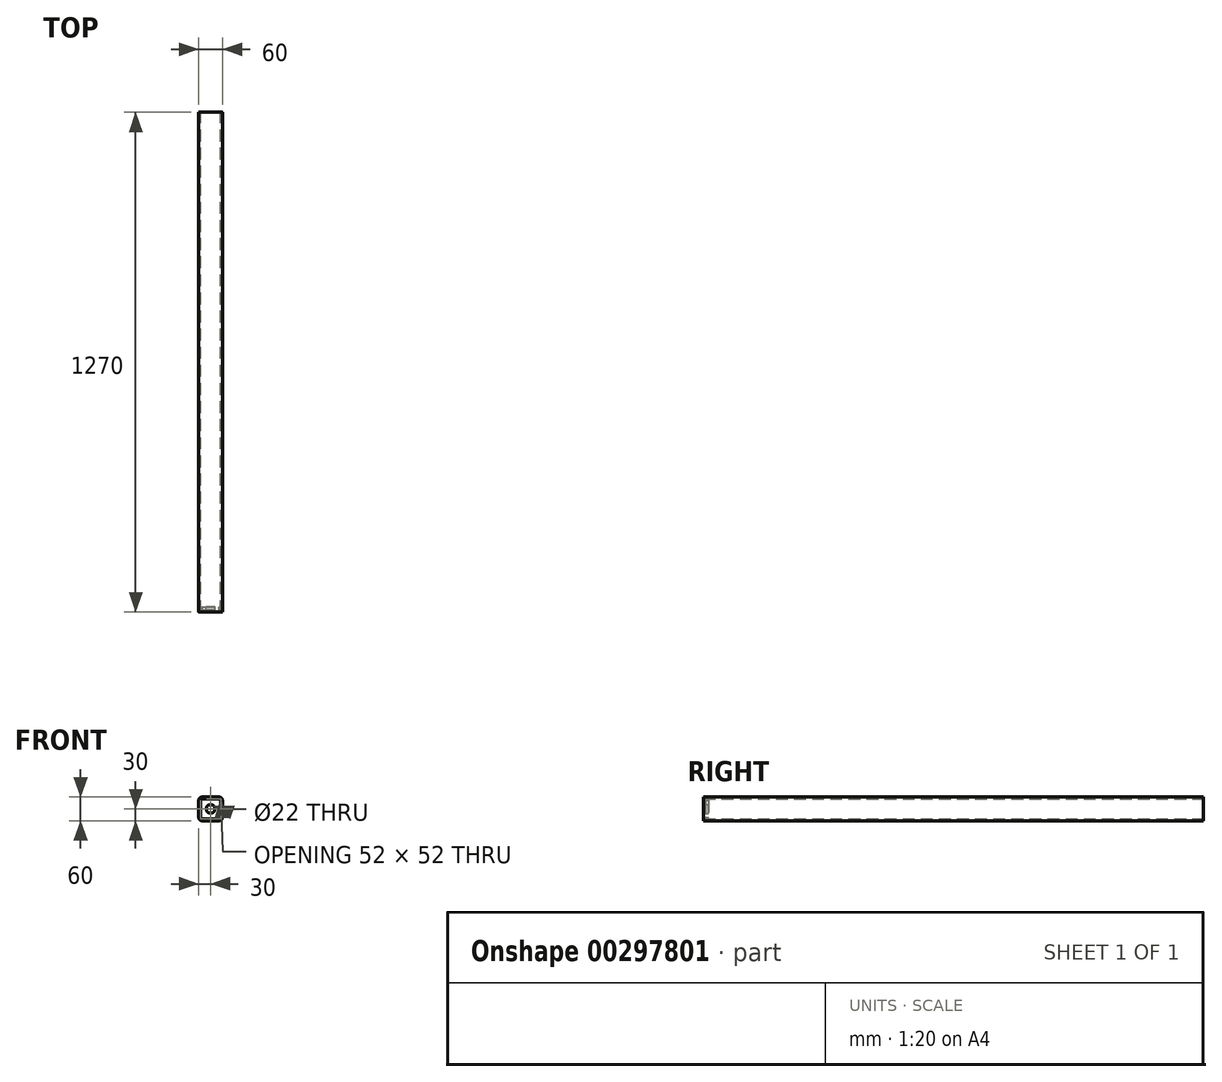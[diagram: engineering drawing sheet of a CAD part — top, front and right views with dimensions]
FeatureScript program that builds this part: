
annotation { "Feature Type Name" : "Feature", "Feature Type Description" : "" }
export const myFeature = defineFeature(function(context is Context, id is Id, definition is map)
    precondition{}
    {
        {
            var Q0;
            Q0=qCreatedBy(makeId("Front.planeOp"),FACE);
            var sketch = newSketch(context, id + "F0", { "sketchPlane" : qUnion([Q0])});
            skLineSegment(sketch, "E0.bottom", {"start": v(-22.05, 30) * mm, "end": v(22.05, 30) * mm});
            skLineSegment(sketch, "E0.top", {"start": v(-22.05, -30) * mm, "end": v(22.05, -30) * mm});
            skLineSegment(sketch, "E0.left", {"start": v(-30, 22.05) * mm, "end": v(-30, -22.05) * mm});
            skLineSegment(sketch, "E0.right", {"start": v(30, 22.05) * mm, "end": v(30, -22.05) * mm});
            skPoint(sketch, "E1.visualSharp", {"position": v(0, 0) * mm});
            skArc(sketch, "E1.filletArc", {"start": v(-22.05, 30) * mm, "mid": v(-27.67, 27.67) * mm, "end": v(-30, 22.05) * mm});
            skPoint(sketch, "E2.visualSharp", {"position": v(30, 30) * mm});
            skArc(sketch, "E2.filletArc", {"start": v(30, 22.05) * mm, "mid": v(27.67, 27.67) * mm, "end": v(22.05, 30) * mm});
            skPoint(sketch, "E3.visualSharp", {"position": v(30, -30) * mm});
            skArc(sketch, "E3.filletArc", {"start": v(22.05, -30) * mm, "mid": v(27.67, -27.67) * mm, "end": v(30, -22.05) * mm});
            skPoint(sketch, "E4.visualSharp", {"position": v(-30, -30) * mm});
            skArc(sketch, "E4.filletArc", {"start": v(-30, -22.05) * mm, "mid": v(-27.67, -27.67) * mm, "end": v(-22.05, -30) * mm});
            skArc(sketch, "E5.0", {"start": v(26, 22.05) * mm, "mid": v(24.84, 24.84) * mm, "end": v(22.05, 26) * mm});
            skLineSegment(sketch, "E5.1", {"start": v(-22.05, 26) * mm, "end": v(22.05, 26) * mm});
            skLineSegment(sketch, "E5.2", {"start": v(26, 22.05) * mm, "end": v(26, -22.05) * mm});
            skArc(sketch, "E5.3", {"start": v(-22.05, 26) * mm, "mid": v(-24.84, 24.84) * mm, "end": v(-26, 22.05) * mm});
            skArc(sketch, "E5.4", {"start": v(22.05, -26) * mm, "mid": v(24.84, -24.84) * mm, "end": v(26, -22.05) * mm});
            skLineSegment(sketch, "E5.5", {"start": v(-22.05, -26) * mm, "end": v(22.05, -26) * mm});
            skArc(sketch, "E5.6", {"start": v(-26, -22.05) * mm, "mid": v(-24.84, -24.84) * mm, "end": v(-22.05, -26) * mm});
            skLineSegment(sketch, "E5.7", {"start": v(-26, 22.05) * mm, "end": v(-26, -22.05) * mm});
            skCircle(sketch, "E6", {"center": v(0, 0) * mm, "radius": 11 * mm});
            skPoint(sketch, "E6.centerSnap0", {"position": v(0, 26) * mm});
            skLineSegment(sketch, "E7", {"start": v(-26, 0) * mm, "end": v(26, 0) * mm, "construction": true});
            skLineSegment(sketch, "E8", {"start": v(-26, 21) * mm, "end": v(-21, 26) * mm});
            skLineSegment(sketch, "E9.1.0", {"start": v(-21, -26) * mm, "end": v(-26, -21) * mm});
            skLineSegment(sketch, "E9.2.0", {"start": v(26, -21) * mm, "end": v(21, -26) * mm});
            skLineSegment(sketch, "E9.3.0", {"start": v(21, 26) * mm, "end": v(26, 21) * mm});
            skSolve(sketch);
        }
        {
            var Q0;
            Q0=makeQuery(id+"F0.imprint","IMPRINT",FACE,{"disambiguationData":[TD([[makeQuery(id+"F0.imprint","IMPRINT",EDGE,{"derivedFrom":sQuery(id+"F0.wireOp",EDGE,"E0.bottom")}),-1.0]])]});
            extrude(context, id + "F1", {"entities" : qUnion([Q0]), "depth" : 1270 * mm, "offsetDistance" : 25 * mm, "symmetric" : true});
        }
        {
            var Q0;
            Q0=makeQuery(id+"F0.imprint","IMPRINT",FACE,{"disambiguationData":[TD([[makeQuery(id+"F0.imprint","IMPRINT",EDGE,{"derivedFrom":sQuery(id+"F0.wireOp",EDGE,"E6")}),-1.0]])]});
            extrude(context, id + "F2", {"entities" : qUnion([Q0]), "depth" : ((1270 / 2) - 5) * mm, "offsetDistance" : 25 * mm, "hasSecondDirection" : true, "secondDirectionOppositeDirection" : false, "secondDirectionDepth" : 622 * mm});
        }
    });
